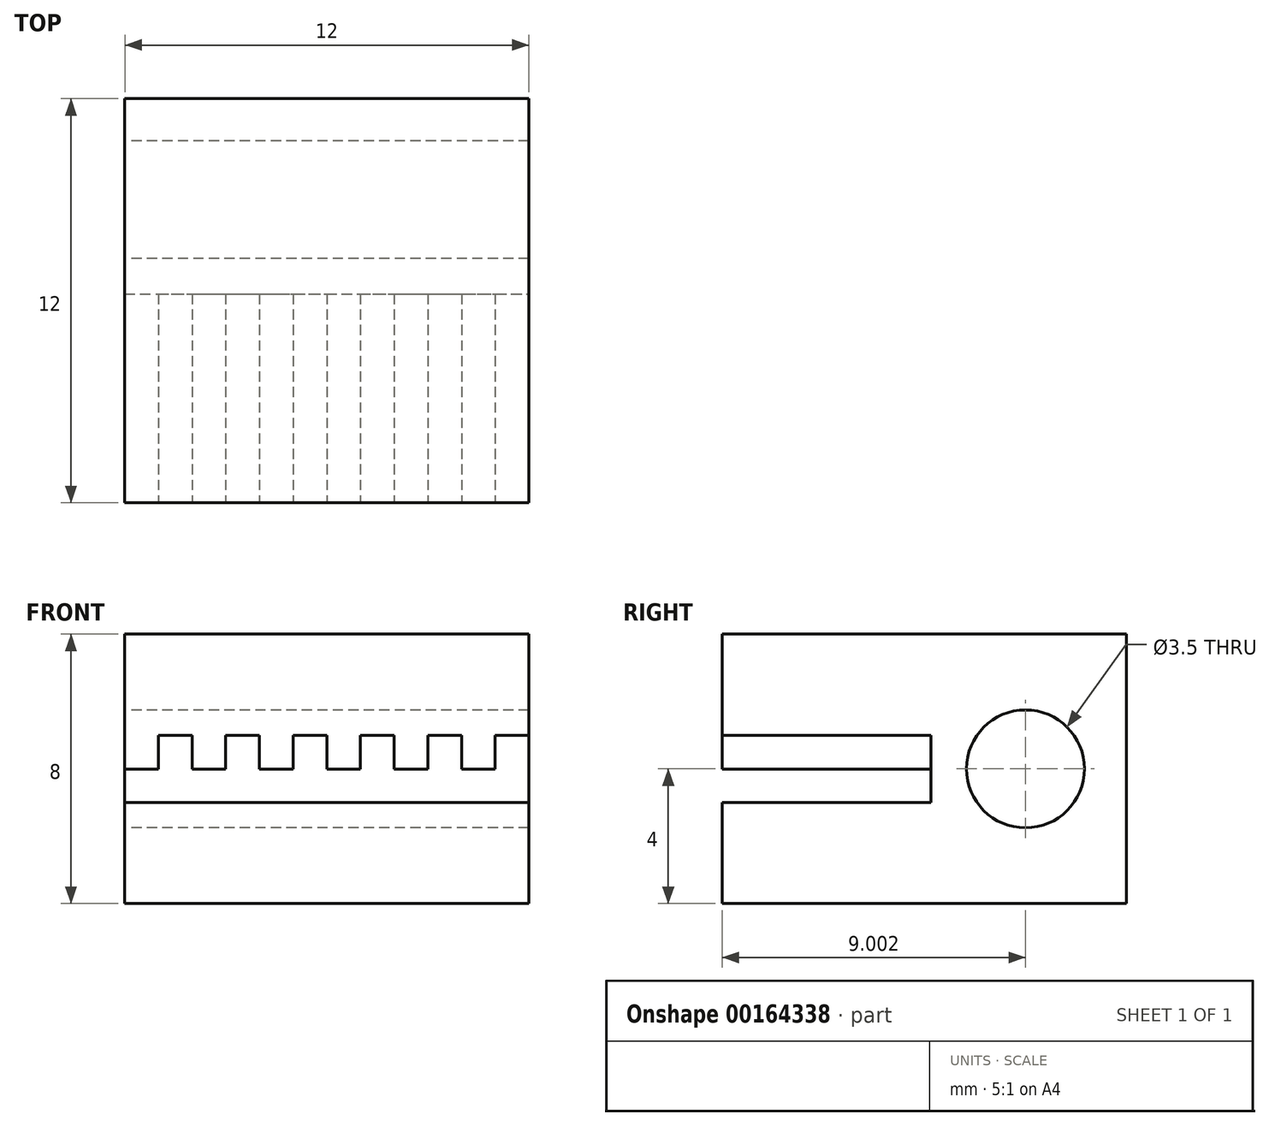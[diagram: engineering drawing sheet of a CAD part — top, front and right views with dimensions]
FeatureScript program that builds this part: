
annotation { "Feature Type Name" : "Feature", "Feature Type Description" : "" }
export const myFeature = defineFeature(function(context is Context, id is Id, definition is map)
    precondition{}
    {
        {
            var Q0;
            Q0=qCreatedBy(makeId("Top.planeOp"),FACE);
            var sketch = newSketch(context, id + "F0", { "sketchPlane" : qUnion([Q0])});
            skLineSegment(sketch, "E0.bottom", {"start": v(6.14, 7.11) * mm, "end": v(18.14, 7.11) * mm});
            skLineSegment(sketch, "E0.top", {"start": v(6.14, -4.89) * mm, "end": v(18.14, -4.89) * mm});
            skLineSegment(sketch, "E0.left", {"start": v(6.14, 7.11) * mm, "end": v(6.14, -4.89) * mm});
            skLineSegment(sketch, "E0.right", {"start": v(18.14, 7.11) * mm, "end": v(18.14, -4.89) * mm});
            skSolve(sketch);
        }
        {
            var Q0;
            Q0 = qSketchRegion(id + "F0", true);
            extrude(context, id + "F1", {"entities" : qUnion([Q0]), "flatOperationType" : FlatOperationType.REMOVE, "offsetDistance" : 25 * mm, "depth" : 8 * mm, "domain" : OperationDomain.MODEL});
        }
        {
            var Q0;
            Q0=makeQuery(id+"F1.opExtrude","SWEPT_FACE",FACE,{"disambiguationData":[OSD([sQuery(id+"F0.wireOp",EDGE,"E0.top")])]});
            var sketch = newSketch(context, id + "F2", { "sketchPlane" : qUnion([Q0])});
            skLineSegment(sketch, "E1", {"start": v(6.14, 3) * mm, "end": v(18.14, 3) * mm});
            skLineSegment(sketch, "E2", {"start": v(6.14, 4) * mm, "end": v(7.14, 4) * mm});
            skLineSegment(sketch, "E3", {"start": v(7.14, 4) * mm, "end": v(7.14, 5) * mm});
            skLineSegment(sketch, "E4", {"start": v(7.14, 5) * mm, "end": v(8.14, 5) * mm});
            skLineSegment(sketch, "E5", {"start": v(8.14, 5) * mm, "end": v(8.14, 4) * mm});
            skLineSegment(sketch, "E6.1.0.0", {"start": v(10.14, 5) * mm, "end": v(10.14, 4) * mm});
            skLineSegment(sketch, "E6.1.0.1", {"start": v(9.14, 5) * mm, "end": v(10.14, 5) * mm});
            skLineSegment(sketch, "E6.1.0.2", {"start": v(9.14, 4) * mm, "end": v(9.14, 5) * mm});
            skLineSegment(sketch, "E6.1.0.3", {"start": v(8.14, 4) * mm, "end": v(9.14, 4) * mm});
            skLineSegment(sketch, "E6.2.0.0", {"start": v(12.14, 5) * mm, "end": v(12.14, 4) * mm});
            skLineSegment(sketch, "E6.2.0.1", {"start": v(11.14, 5) * mm, "end": v(12.14, 5) * mm});
            skLineSegment(sketch, "E6.2.0.2", {"start": v(11.14, 4) * mm, "end": v(11.14, 5) * mm});
            skLineSegment(sketch, "E6.2.0.3", {"start": v(10.14, 4) * mm, "end": v(11.14, 4) * mm});
            skLineSegment(sketch, "E6.3.0.0", {"start": v(14.14, 5) * mm, "end": v(14.14, 4) * mm});
            skLineSegment(sketch, "E6.3.0.1", {"start": v(13.14, 5) * mm, "end": v(14.14, 5) * mm});
            skLineSegment(sketch, "E6.3.0.2", {"start": v(13.14, 4) * mm, "end": v(13.14, 5) * mm});
            skLineSegment(sketch, "E6.3.0.3", {"start": v(12.14, 4) * mm, "end": v(13.14, 4) * mm});
            skLineSegment(sketch, "E6.direction1", {"start": v(6.14, 4) * mm, "end": v(8.14, 4) * mm, "construction": true});
            skLineSegment(sketch, "E7", {"start": v(14.14, 4) * mm, "end": v(15.14, 4) * mm});
            skLineSegment(sketch, "E8", {"start": v(15.14, 4) * mm, "end": v(15.14, 5) * mm});
            skLineSegment(sketch, "E9", {"start": v(15.14, 5) * mm, "end": v(16.14, 5) * mm});
            skLineSegment(sketch, "E10", {"start": v(16.14, 5) * mm, "end": v(16.14, 4) * mm});
            skLineSegment(sketch, "E11", {"start": v(16.14, 4) * mm, "end": v(17.14, 4) * mm});
            skLineSegment(sketch, "E12", {"start": v(17.14, 4) * mm, "end": v(17.14, 5) * mm});
            skLineSegment(sketch, "E13", {"start": v(17.14, 5) * mm, "end": v(18.14, 5) * mm});
            skSolve(sketch);
        }
        {
            var Q0;
            {var subQ1=sQuery(id+"F2.wireOp",EDGE,"E1");Q0=makeQuery(id+"F2.imprint","IMPRINT",FACE,{"disambiguationData":[TD([[makeQuery(id+"F2.imprint","IMPRINT",EDGE,{"derivedFrom":subQ1}),1.0]])]});}
            extrude(context, id + "F3", {"entities" : qUnion([Q0]), "operationType" : NewBodyOperationType.REMOVE, "oppositeDirection" : true, "depth" : 6.2 * mm});
        }
        {
            var Q0;
            Q0=makeQuery(id+"F1.opExtrude","SWEPT_FACE",FACE,{"disambiguationData":[OSD([sQuery(id+"F0.wireOp",EDGE,"E0.left")])]});
            var sketch = newSketch(context, id + "F4", { "sketchPlane" : qUnion([Q0])});
            skCircle(sketch, "E14", {"center": v(-4.11, 4) * mm, "radius": 1.75 * mm});
            skPoint(sketch, "E14.centerSnap0", {"position": v(-7.11, 4) * mm});
            skSolve(sketch);
        }
        {
            var Q0;
            Q0 = qSketchRegion(id + "F4", true);
            extrude(context, id + "F5", {"entities" : qUnion([Q0]), "operationType" : NewBodyOperationType.REMOVE, "oppositeDirection" : true, "depth" : 25 * mm});
        }
    });
